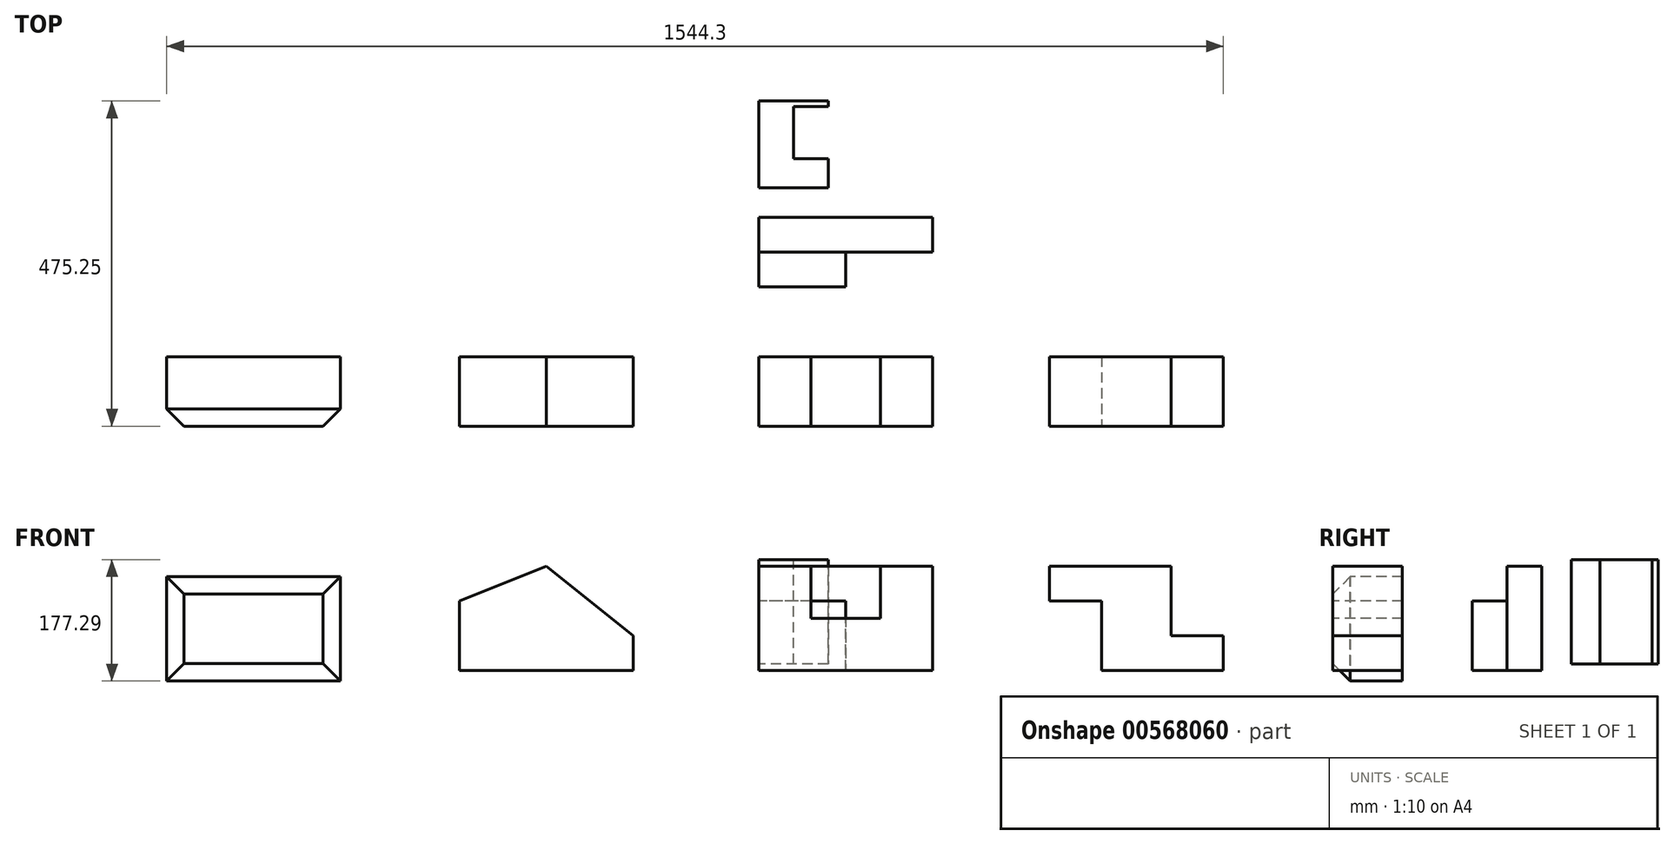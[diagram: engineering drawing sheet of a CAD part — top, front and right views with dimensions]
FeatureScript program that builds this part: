
annotation { "Feature Type Name" : "Feature", "Feature Type Description" : "" }
export const myFeature = defineFeature(function(context is Context, id is Id, definition is map)
    precondition{}
    {
        {
            var Q0;
            Q0=qCreatedBy(makeId("Front.planeOp"),FACE);
            var sketch = newSketch(context, id + "F0", { "sketchPlane" : qUnion([Q0])});
            skLineSegment(sketch, "E0", {"start": v(0, 0) * mm, "end": v(0, 152.4) * mm});
            skLineSegment(sketch, "E1", {"start": v(0, 152.4) * mm, "end": v(76.2, 152.4) * mm});
            skLineSegment(sketch, "E2", {"start": v(76.2, 152.4) * mm, "end": v(76.2, 76.2) * mm});
            skLineSegment(sketch, "E3", {"start": v(76.2, 76.2) * mm, "end": v(177.8, 76.2) * mm});
            skLineSegment(sketch, "E4", {"start": v(177.8, 76.2) * mm, "end": v(177.8, 152.4) * mm});
            skLineSegment(sketch, "E5", {"start": v(177.8, 152.4) * mm, "end": v(254, 152.4) * mm});
            skLineSegment(sketch, "E6", {"start": v(254, 152.4) * mm, "end": v(254, 0) * mm});
            skLineSegment(sketch, "E7", {"start": v(254, 0) * mm, "end": v(0, 0) * mm});
            skSolve(sketch);
        }
        {
            var Q0;
            Q0=makeQuery(id+"F0.imprint","IMPRINT",FACE,{"disambiguationData":[TD([[makeQuery(id+"F0.imprint","IMPRINT",EDGE,{"derivedFrom":sQuery(id+"F0.wireOp",EDGE,"E0")}),-1.0]])]});
            extrude(context, id + "F1", {"entities" : qUnion([Q0]), "oppositeDirection" : true, "depth" : 101.6 * mm, "offsetDistance" : 25.4 * mm});
        }
        {
            var Q0;
            Q0=qCreatedBy(makeId("Right.planeOp"),FACE);
            var sketch = newSketch(context, id + "F2", { "sketchPlane" : qUnion([Q0])});
            skLineSegment(sketch, "E8", {"start": v(203.62, 0) * mm, "end": v(203.62, 101.6) * mm});
            skLineSegment(sketch, "E9", {"start": v(203.62, 101.6) * mm, "end": v(254.42, 101.6) * mm});
            skLineSegment(sketch, "E10", {"start": v(254.42, 101.6) * mm, "end": v(254.42, 152.4) * mm});
            skLineSegment(sketch, "E11", {"start": v(254.42, 152.4) * mm, "end": v(305.22, 152.4) * mm});
            skLineSegment(sketch, "E12", {"start": v(305.22, 152.4) * mm, "end": v(305.22, 0) * mm});
            skLineSegment(sketch, "E13", {"start": v(305.22, 0) * mm, "end": v(203.62, 0) * mm});
            skSolve(sketch);
        }
        {
            var Q0;
            Q0=makeQuery(id+"F2.imprint","IMPRINT",FACE,{"disambiguationData":[TD([[makeQuery(id+"F2.imprint","IMPRINT",EDGE,{"derivedFrom":sQuery(id+"F2.wireOp",EDGE,"E8")}),-1.0]])]});
            extrude(context, id + "F3", {"entities" : qUnion([Q0]), "depth" : 254 * mm, "offsetDistance" : 25.4 * mm});
        }
        {
            var Q0;
            Q0=makeQuery(id+"F3.opExtrude","CAP_FACE",FACE,{"disambiguationData":[OSD([sQuery(id+"F2.wireOp",EDGE,"E8"),sQuery(id+"F2.wireOp",EDGE,"E9"),sQuery(id+"F2.wireOp",EDGE,"E10"),sQuery(id+"F2.wireOp",EDGE,"E11"),sQuery(id+"F2.wireOp",EDGE,"E12"),sQuery(id+"F2.wireOp",EDGE,"E13")])],"isStart":false});
            var sketch = newSketch(context, id + "F4", { "sketchPlane" : qUnion([Q0])});
            skLineSegment(sketch, "E14.bottom", {"start": v(203.62, 101.6) * mm, "end": v(254.42, 101.6) * mm});
            skLineSegment(sketch, "E14.top", {"start": v(203.62, 0) * mm, "end": v(254.42, 0) * mm});
            skLineSegment(sketch, "E14.left", {"start": v(203.62, 101.6) * mm, "end": v(203.62, 0) * mm});
            skLineSegment(sketch, "E14.right", {"start": v(254.42, 101.6) * mm, "end": v(254.42, 0) * mm});
            skSolve(sketch);
        }
        {
            var Q0;
            Q0=makeQuery(id+"F4.imprint","IMPRINT",FACE,{"disambiguationData":[TD([[makeQuery(id+"F4.imprint","IMPRINT",EDGE,{"derivedFrom":sQuery(id+"F4.wireOp",EDGE,"E14.bottom")}),-1.0]])]});
            extrude(context, id + "F5", {"entities" : qUnion([Q0]), "operationType" : NewBodyOperationType.REMOVE, "oppositeDirection" : true, "depth" : 127 * mm, "offsetDistance" : 25.4 * mm});
        }
        {
            var Q0;
            Q0=qCreatedBy(makeId("Right.planeOp"),FACE);
            var sketch = newSketch(context, id + "F6", { "sketchPlane" : qUnion([Q0])});
            skLineSegment(sketch, "E15", {"start": v(348.26, 161.99) * mm, "end": v(526.06, 161.99) * mm});
            skLineSegment(sketch, "E16", {"start": v(526.06, 161.99) * mm, "end": v(526.06, 60.39) * mm});
            skLineSegment(sketch, "E17", {"start": v(526.06, 60.39) * mm, "end": v(602.26, 60.39) * mm});
            skLineSegment(sketch, "E18", {"start": v(602.26, 60.39) * mm, "end": v(602.26, 9.59) * mm});
            skLineSegment(sketch, "E19", {"start": v(348.26, 161.99) * mm, "end": v(348.26, 9.59) * mm});
            skLineSegment(sketch, "E20", {"start": v(348.26, 9.59) * mm, "end": v(602.26, 9.59) * mm});
            skLineSegment(sketch, "E21", {"start": v(348.26, 161.99) * mm, "end": v(399.06, 161.99) * mm});
            skLineSegment(sketch, "E22", {"start": v(399.06, 161.99) * mm, "end": v(399.06, 9.59) * mm});
            skLineSegment(sketch, "E23", {"start": v(399.06, 161.99) * mm, "end": v(475.25, 161.99) * mm});
            skLineSegment(sketch, "E24", {"start": v(475.25, 161.99) * mm, "end": v(475.25, 9.59) * mm});
            skSolve(sketch);
        }
        {
            var Q0;
            {var subQ0=sQuery(id+"F6.wireOp",EDGE,"E22");Q0=makeQuery(id+"F6.imprint","IMPRINT",FACE,{"disambiguationData":[TD([[makeQuery(id+"F6.imprint","IMPRINT",EDGE,{"derivedFrom":subQ0}),1.0]])]});}
            var Q1;
            {var subQ0=sQuery(id+"F6.wireOp",EDGE,"E19");Q1=makeQuery(id+"F6.imprint","IMPRINT",FACE,{"disambiguationData":[TD([[makeQuery(id+"F6.imprint","IMPRINT",EDGE,{"derivedFrom":subQ0}),1.0]])]});}
            var Q2;
            Q2=makeQuery(id+"F6.imprint","IMPRINT",FACE,{"disambiguationData":[TD([[makeQuery(id+"F6.imprint","IMPRINT",EDGE,{"derivedFrom":sQuery(id+"F6.wireOp",EDGE,"E15")}),-1.0]])]});
            extrude(context, id + "F7", {"entities" : qUnion([Q0, Q1, Q2]), "depth" : 101.6 * mm, "offsetDistance" : 25.4 * mm});
        }
        {
            var Q0;
            Q0=makeQuery(id+"F7.opExtrude","SWEPT_FACE",FACE,{"disambiguationData":[OSD([sQuery(id+"F6.wireOp",EDGE,"E15"),sQuery(id+"F6.wireOp",EDGE,"E21"),sQuery(id+"F6.wireOp",EDGE,"E23")])]});
            var sketch = newSketch(context, id + "F8", { "sketchPlane" : qUnion([Q0])});
            skLineSegment(sketch, "E25.bottom", {"start": v(101.6, 466.8) * mm, "end": v(50.8, 466.8) * mm});
            skLineSegment(sketch, "E25.top", {"start": v(101.6, 390.6) * mm, "end": v(50.8, 390.6) * mm});
            skLineSegment(sketch, "E25.left", {"start": v(101.6, 466.8) * mm, "end": v(101.6, 390.6) * mm});
            skLineSegment(sketch, "E25.right", {"start": v(50.8, 466.8) * mm, "end": v(50.8, 390.6) * mm});
            skSolve(sketch);
        }
        {
            var Q0;
            Q0=makeQuery(id+"F8.imprint","IMPRINT",FACE,{"disambiguationData":[TD([[makeQuery(id+"F8.imprint","IMPRINT",EDGE,{"derivedFrom":sQuery(id+"F8.wireOp",EDGE,"E25.bottom")}),1.0]])]});
            extrude(context, id + "F9", {"entities" : qUnion([Q0]), "operationType" : NewBodyOperationType.REMOVE, "oppositeDirection" : true, "depth" : 152.4 * mm, "offsetDistance" : 25.4 * mm});
        }
        {
            var Q0;
            Q0=qCreatedBy(makeId("Front.planeOp"),FACE);
            var sketch = newSketch(context, id + "F10", { "sketchPlane" : qUnion([Q0])});
            skLineSegment(sketch, "E26", {"start": v(425.04, 152.4) * mm, "end": v(425.04, 101.6) * mm});
            skLineSegment(sketch, "E27", {"start": v(425.04, 101.6) * mm, "end": v(501.24, 101.6) * mm});
            skLineSegment(sketch, "E28", {"start": v(501.24, 101.6) * mm, "end": v(501.24, 0) * mm});
            skLineSegment(sketch, "E29", {"start": v(501.24, 0) * mm, "end": v(679.04, 0) * mm});
            skLineSegment(sketch, "E30", {"start": v(679.04, 0) * mm, "end": v(679.04, 50.8) * mm});
            skLineSegment(sketch, "E31", {"start": v(679.04, 50.8) * mm, "end": v(602.84, 50.8) * mm});
            skLineSegment(sketch, "E32", {"start": v(602.84, 50.8) * mm, "end": v(602.84, 152.4) * mm});
            skLineSegment(sketch, "E33", {"start": v(602.84, 152.4) * mm, "end": v(425.04, 152.4) * mm});
            skSolve(sketch);
        }
        {
            var Q0;
            Q0=makeQuery(id+"F10.imprint","IMPRINT",FACE,{"disambiguationData":[TD([[makeQuery(id+"F10.imprint","IMPRINT",EDGE,{"derivedFrom":sQuery(id+"F10.wireOp",EDGE,"E26")}),1.0]])]});
            extrude(context, id + "F11", {"entities" : qUnion([Q0]), "oppositeDirection" : true, "depth" : 101.6 * mm, "offsetDistance" : 25.4 * mm});
        }
        {
            var Q0;
            Q0=qCreatedBy(makeId("Front.planeOp"),FACE);
            var sketch = newSketch(context, id + "F12", { "sketchPlane" : qUnion([Q0])});
            skLineSegment(sketch, "E34", {"start": v(-183.67, 0) * mm, "end": v(-437.67, 0) * mm});
            skLineSegment(sketch, "E35", {"start": v(-437.67, 0) * mm, "end": v(-437.67, 101.6) * mm});
            skLineSegment(sketch, "E36", {"start": v(-183.67, 0) * mm, "end": v(-183.67, 50.8) * mm});
            skPoint(sketch, "E37.startSnap0", {"position": v(-310.67, 0) * mm});
            skLineSegment(sketch, "E38", {"start": v(-437.67, 101.6) * mm, "end": v(-310.67, 152.4) * mm});
            skLineSegment(sketch, "E39", {"start": v(-310.67, 152.4) * mm, "end": v(-183.67, 50.8) * mm});
            skSolve(sketch);
        }
        {
            var Q0;
            Q0=makeQuery(id+"F12.imprint","IMPRINT",FACE,{"disambiguationData":[TD([[makeQuery(id+"F12.imprint","IMPRINT",EDGE,{"derivedFrom":sQuery(id+"F12.wireOp",EDGE,"E34")}),-1.0]])]});
            extrude(context, id + "F13", {"entities" : qUnion([Q0]), "oppositeDirection" : true, "depth" : 101.6 * mm, "offsetDistance" : 25.4 * mm});
        }
        {
            var Q0;
            Q0=qCreatedBy(makeId("Front.planeOp"),FACE);
            var sketch = newSketch(context, id + "F14", { "sketchPlane" : qUnion([Q0])});
            skLineSegment(sketch, "E40.bottom", {"start": v(-865.26, 137.1) * mm, "end": v(-611.26, 137.1) * mm});
            skLineSegment(sketch, "E40.top", {"start": v(-865.26, -15.3) * mm, "end": v(-611.26, -15.3) * mm});
            skLineSegment(sketch, "E40.left", {"start": v(-865.26, 137.1) * mm, "end": v(-865.26, -15.3) * mm});
            skLineSegment(sketch, "E40.right", {"start": v(-611.26, 137.1) * mm, "end": v(-611.26, -15.3) * mm});
            skSolve(sketch);
        }
        {
            var Q0;
            Q0=makeQuery(id+"F14.imprint","IMPRINT",FACE,{"disambiguationData":[TD([[makeQuery(id+"F14.imprint","IMPRINT",EDGE,{"derivedFrom":sQuery(id+"F14.wireOp",EDGE,"E40.bottom")}),-1.0]])]});
            extrude(context, id + "F15", {"entities" : qUnion([Q0]), "oppositeDirection" : true, "depth" : 101.6 * mm, "offsetDistance" : 25.4 * mm});
        }
        {
            var Q0;
            Q0=makeQuery(id+"F15.opExtrude","CAP_FACE",FACE,{"disambiguationData":[OSD([sQuery(id+"F14.wireOp",EDGE,"E40.bottom"),sQuery(id+"F14.wireOp",EDGE,"E40.top"),sQuery(id+"F14.wireOp",EDGE,"E40.left"),sQuery(id+"F14.wireOp",EDGE,"E40.right")])],"isStart":true});
            chamfer(context, id + "F16", {"entities" : qUnion([Q0]), "width" : 25.4 * mm, "tangentPropagation" : true});
        }
    });
